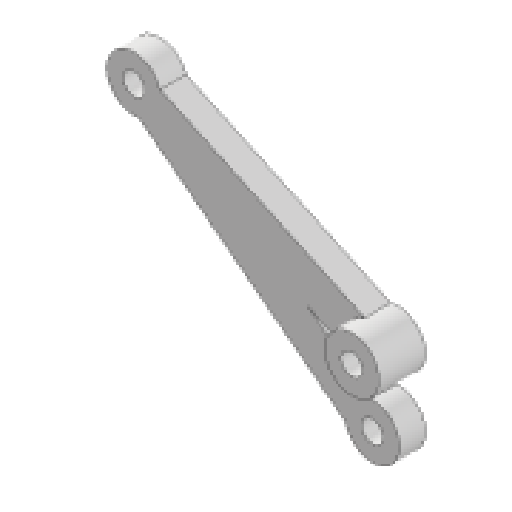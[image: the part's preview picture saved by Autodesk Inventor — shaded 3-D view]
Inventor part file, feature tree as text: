
AUTODESK INVENTOR PART (.ipt)
format: ipt  version: 2025 (Build 290162010, 162A)  size: 131,072 bytes
history: native  units: in
note: dims shown in document units (in); Inventor stores cm internally (conversion verified against a paired STEP export)
features: extrude x2, sketch x2
ambient origin geometry x8: Origin, YZ Plane, XZ Plane, XY Plane, X Axis, Y Axis, Z Axis, Center Point
bodies: Solid1 (feature_tree)
feature tree (4):
  extrude  "Extrusion1"  Depth=0.16in
  extrude  "Extrusion4"  Depth=0.15in
  sketch  "Sketch1"  dims[d0=0.4in d1=0.16in]
  sketch  "Sketch4"  dims[d7=0.4in d8=0.16in d9=0.5in d10=0.3in d11=0.15in d12=60.0deg d14=0.19in d15=0.0in d20=0.4in d21=0.16in d25=0.3in d29=1.75in d30=0.3in d31=0.15in d32=1.0in d33=0.1718in d34=0.15in d35=0.0in]
